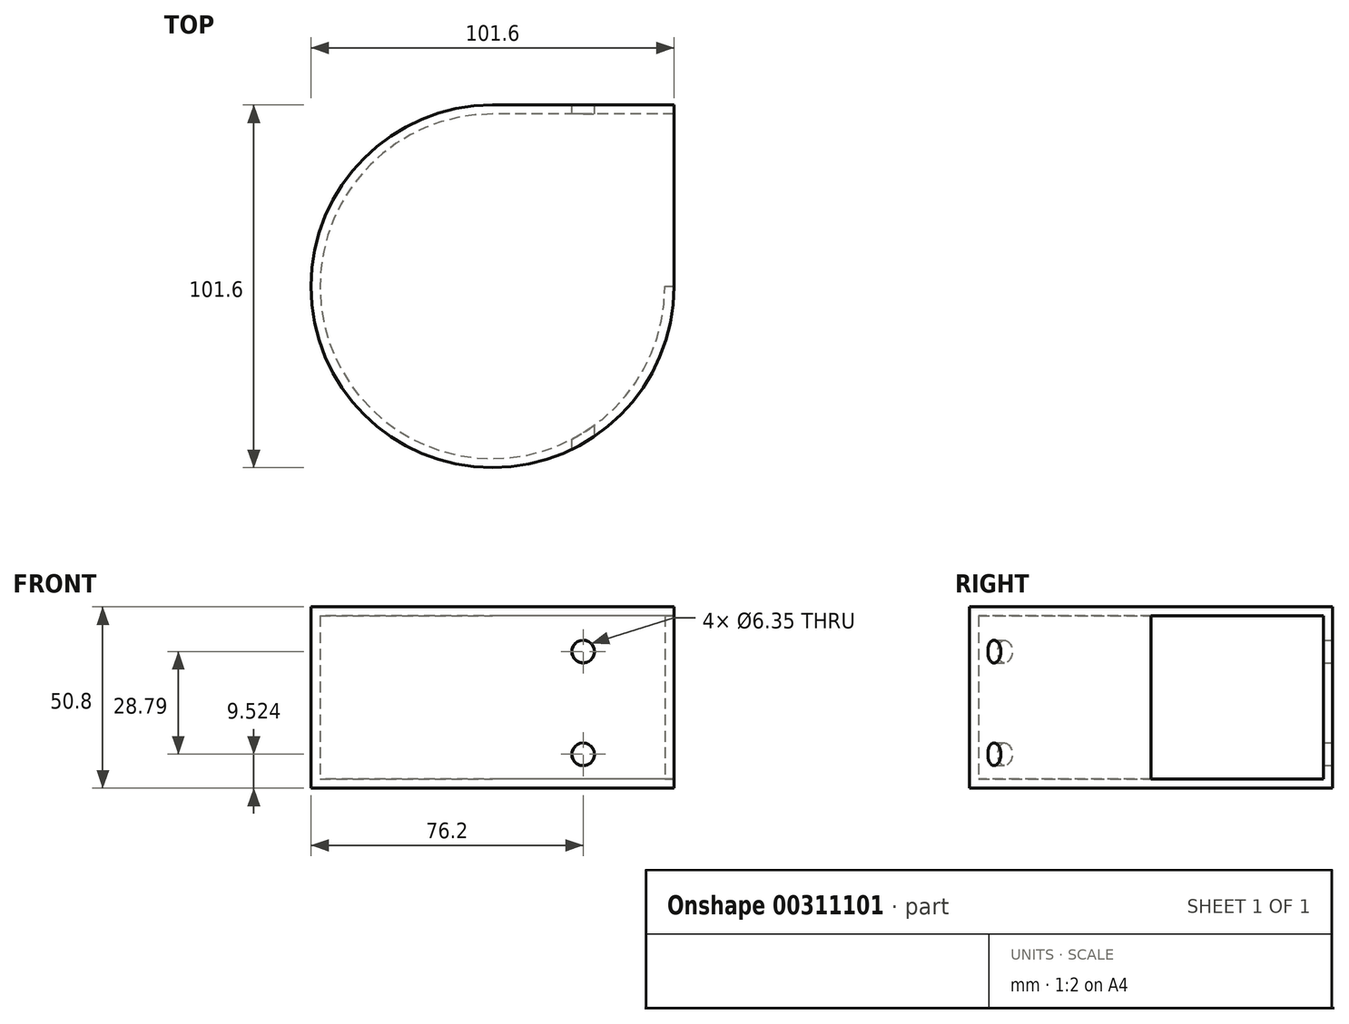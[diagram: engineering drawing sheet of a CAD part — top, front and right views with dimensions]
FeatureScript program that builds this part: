
annotation { "Feature Type Name" : "Feature", "Feature Type Description" : "" }
export const myFeature = defineFeature(function(context is Context, id is Id, definition is map)
    precondition{}
    {
        {
            var Q0;
            Q0=qCreatedBy(makeId("Front.planeOp"),FACE);
            var sketch = newSketch(context, id + "F0", { "sketchPlane" : qUnion([Q0])});
            skLineSegment(sketch, "E0.bottom", {"start": v(25.4, -25.4) * mm, "end": v(-25.4, -25.4) * mm});
            skLineSegment(sketch, "E0.top", {"start": v(25.4, 25.4) * mm, "end": v(-25.4, 25.4) * mm});
            skLineSegment(sketch, "E0.left", {"start": v(25.4, -25.4) * mm, "end": v(25.4, 25.4) * mm});
            skLineSegment(sketch, "E0.right", {"start": v(-25.4, -25.4) * mm, "end": v(-25.4, 25.4) * mm});
            skPoint(sketch, "E0.middle", {"position": v(0, 0) * mm});
            skPoint(sketch, "E1", {"position": v(0, 12.7) * mm});
            skPoint(sketch, "E2", {"position": v(0, -12.7) * mm});
            skSolve(sketch);
        }
        {
            var Q0;
            Q0 = qSketchRegion(id + "F0", true);
            extrude(context, id + "F1", {"entities" : qUnion([Q0]), "endBound" : BoundingType.SYMMETRIC, "depth" : 50.8 * mm});
        }
        {
            var Q0;
            Q0=makeQuery(id+"F1.opExtrude","CAP_FACE",FACE,{"disambiguationData":[OSD([sQuery(id+"F0.wireOp",EDGE,"E0.bottom"),sQuery(id+"F0.wireOp",EDGE,"E0.top"),sQuery(id+"F0.wireOp",EDGE,"E0.left"),sQuery(id+"F0.wireOp",EDGE,"E0.right")])],"isStart":false});
            var Q1;
            Q1=makeQuery(id+"F1.opExtrude","CAP_EDGE",EDGE,{"disambiguationData":[OSD([sQuery(id+"F0.wireOp",EDGE,"E0.right")])],"isStart":false});
            revolve(context, id + "F2", {"operationType" : NewBodyOperationType.ADD, "entities" : qUnion([Q0]), "axis" : qUnion([Q1]), "revolveType" : RevolveType.FULL});
        }
        {
            var Q0;
            Q0=makeQuery(id+"F1.opExtrude","SWEPT_FACE",FACE,{"disambiguationData":[OSD([sQuery(id+"F0.wireOp",EDGE,"E0.left")])]});
            shell(context, id + "F3", {"entities" : qUnion([Q0]), "thickness" : 2.54 * mm});
        }
        {
            var Q0;
            Q0=makeQuery(id+"F1.opExtrude","CAP_FACE",FACE,{"disambiguationData":[OSD([sQuery(id+"F0.wireOp",EDGE,"E0.bottom"),sQuery(id+"F0.wireOp",EDGE,"E0.top"),sQuery(id+"F0.wireOp",EDGE,"E0.left"),sQuery(id+"F0.wireOp",EDGE,"E0.right")])],"isStart":true});
            var sketch = newSketch(context, id + "F4", { "sketchPlane" : qUnion([Q0])});
            skPoint(sketch, "E3", {"position": v(0, 12.91) * mm});
            skPoint(sketch, "E4", {"position": v(0, -15.88) * mm});
            skSolve(sketch);
        }
        {
            var Q0;
            Q0=sQuery(id+"F4.wireOp",VERTEX,"E3");
            var Q1;
            Q1=sQuery(id+"F4.wireOp",VERTEX,"E4");
            var Q2;
            Q2=makeQuery(id+"F1.opExtrude","SWEPT_BODY",BODY,{"disambiguationData":[OSD([sQuery(id+"F0.wireOp",EDGE,"E0.bottom"),sQuery(id+"F0.wireOp",EDGE,"E0.top"),sQuery(id+"F0.wireOp",EDGE,"E0.left"),sQuery(id+"F0.wireOp",EDGE,"E0.right")])]});
            hole(context, id + "F5", {"style" : HoleStyle.SIMPLE, "endStyle" : HoleEndStyle.THROUGH, "holeDiameter" : 6.35 * mm, "tappedDepth" : 12.7 * mm, "tapClearance" : 3, "locations" : qUnion([Q0, Q1]), "scope" : qUnion([Q2])});
        }
    });
